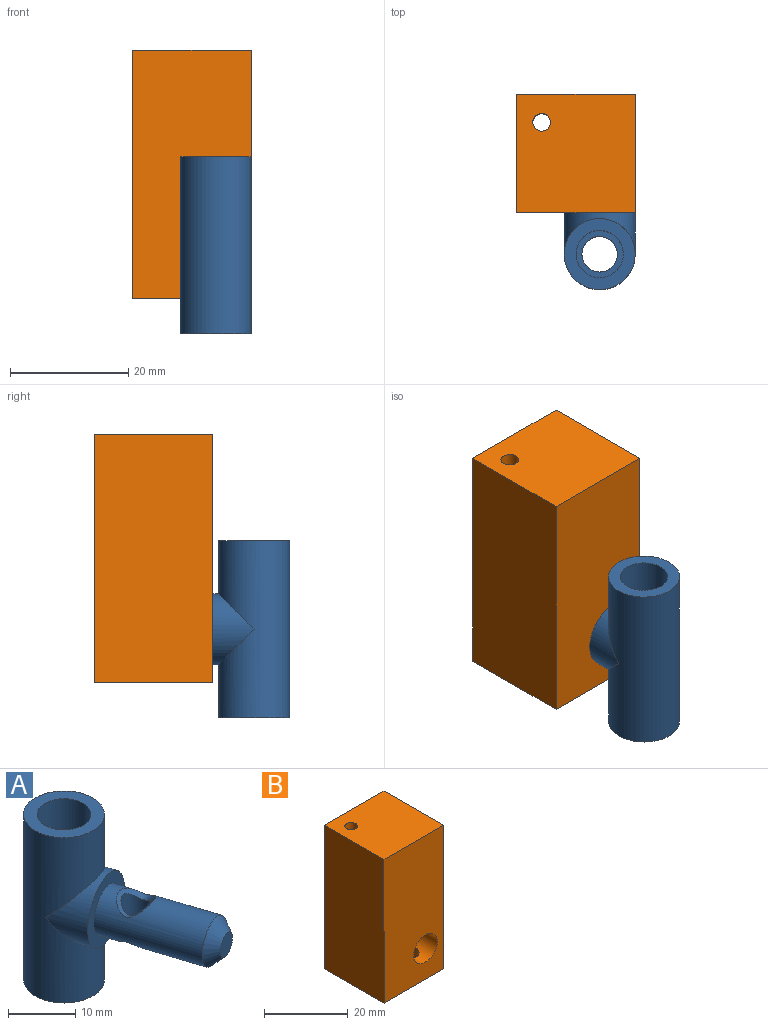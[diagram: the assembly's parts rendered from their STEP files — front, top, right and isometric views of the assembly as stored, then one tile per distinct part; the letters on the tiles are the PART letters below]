
ASSEMBLY  parts=2 mates=1
PART A: 17 faces, bbox 17.9x32.7x30.8 mm
  f0: cylinder r=3mm len=6mm, axis (0,0,-1), area 30.5mm2, adj f4,f10,f11,f12,f13
  f1: cylinder r=4mm len=25mm, axis (0,0,-1), area 628.3mm2, adj f3,f10
  f2: cylinder r=6mm len=30mm, axis (0,0,-1), area 987mm2, adj f3,f4,f8
  f3: plane 12x12mm, normal (0,0,1), area 62.8mm2, adj f1,f2
  f4: plane 12.38x12.38mm, normal (0,0,-1), area 80.2mm2, adj f0,f2,f12,f13
  f5: plane 12x11.41mm, normal (0.31,-0.95,0), area 62.8mm2, adj f6,f8
  f6: cylinder r=4mm len=19.59mm, axis (0.31,-0.95,0), area 387.3mm2, adj f5,f9,f15,f16
  f7: plane 4x3.8mm, normal (0.31,-0.95,0), area 12.6mm2, adj f9
  f8: cylinder r=6mm len=13.58mm, axis (0.31,-0.95,0), area 119.9mm2, adj f2,f5
  f9: cone r=2mm half-angle=45deg, axis (-0.31,0.95,0), area 53.3mm2, adj f6,f7
  f10: plane 8x8mm, normal (0,0,1), area 22mm2, adj f0,f1
  f11: plane 0.73x0.63mm, normal (0,-1,0), area 0.2mm2, adj f0,f12,f13
  f12: bspline ~8.38x7.26mm, area 72.8mm2, adj f0,f4,f11,f13
  f13: bspline ~8.38x7.26mm, area 67.5mm2, adj f0,f4,f11,f12
  f14: cylinder r=2.25mm len=4.5mm, axis (0,0,-1), area 63.1mm2, adj f15,f16
  f15: bspline ~6.55x5.76mm, area 17.2mm2, adj f6,f14
  f16: bspline ~6.49x5.73mm, area 17.2mm2, adj f6,f14
PART B: 11 faces, bbox 20x20x42 mm
  f0: plane 42x20mm, normal (-1,0,0), area 840mm2, adj f1,f3,f5,f6
  f1: plane 20x20mm, normal (0,0,-1), area 380.4mm2, adj f0,f2,f5,f6,f7,f10
  f2: plane 42x20mm, normal (1,0,0), area 840mm2, adj f1,f3,f5,f6
  f3: plane 20x20mm, normal (0,0,1), area 392.9mm2, adj f0,f2,f5,f6,f10
  f4: cylinder r=4mm len=20mm, axis (0,1,0), area 476.7mm2, adj f5,f6,f7,f8
  f5: plane 42x20mm, normal (0,-1,0), area 789.7mm2, adj f0,f1,f2,f3,f4
  f6: plane 42x20mm, normal (0,1,0), area 789.7mm2, adj f0,f1,f2,f3,f4
  f7: cylinder r=2mm len=5.54mm, axis (0,0,-1), area 66.1mm2, adj f1,f4
  f8: cylinder r=2mm len=24.54mm, axis (0,0,-1), area 304.9mm2, adj f4,f9
  f9: plane 4x4mm, normal (0,0,-1), area 12.6mm2, adj f8
  f10: cylinder r=1.5mm len=42mm, axis (0,0,1), area 395.8mm2, adj f1,f3
PLACE A rot(axis=(0,0,1),162deg) t=(-19.38,-25.04,-0.16)mm
PLACE B t=(-33.38,1.96,-14.16)mm fixed
MATE slider A.f9 <-> B.f4  axis (0,1,0) through (-19.38,-18.04,-5.16)mm
